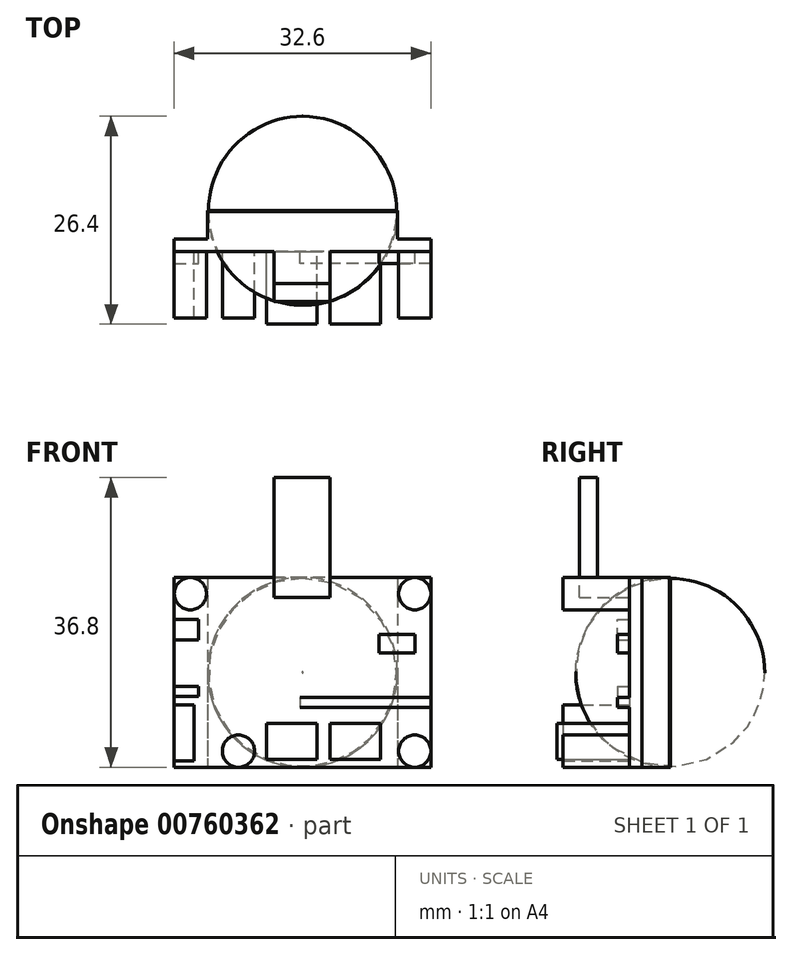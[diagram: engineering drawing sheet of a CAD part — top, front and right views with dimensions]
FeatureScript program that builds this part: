
annotation { "Feature Type Name" : "Feature", "Feature Type Description" : "" }
export const myFeature = defineFeature(function(context is Context, id is Id, definition is map)
    precondition{}
    {
        {
            var Q0;
            Q0=qCreatedBy(makeId("Front.planeOp"),FACE);
            var sketch = newSketch(context, id + "F0", { "sketchPlane" : qUnion([Q0])});
            skLineSegment(sketch, "E0.bottom", {"start": v(16.3, 12.05) * mm, "end": v(-16.3, 12.05) * mm});
            skLineSegment(sketch, "E0.top", {"start": v(16.3, -12.05) * mm, "end": v(-16.3, -12.05) * mm});
            skLineSegment(sketch, "E0.left", {"start": v(16.3, 12.05) * mm, "end": v(16.3, -12.05) * mm});
            skLineSegment(sketch, "E0.right", {"start": v(-16.3, 12.05) * mm, "end": v(-16.3, -12.05) * mm});
            skPoint(sketch, "E0.middle", {"position": v(0, 0) * mm});
            skLineSegment(sketch, "E1.bottom", {"start": v(12.05, 12.05) * mm, "end": v(-12.05, 12.05) * mm});
            skLineSegment(sketch, "E1.top", {"start": v(12.05, -12.05) * mm, "end": v(-12.05, -12.05) * mm});
            skLineSegment(sketch, "E1.left", {"start": v(12.05, 12.05) * mm, "end": v(12.05, -12.05) * mm});
            skLineSegment(sketch, "E1.right", {"start": v(-12.05, 12.05) * mm, "end": v(-12.05, -12.05) * mm});
            skCircle(sketch, "E2", {"center": v(0, 0) * mm, "radius": 12.05 * mm});
            skSolve(sketch);
        }
        {
            var Q0;
            Q0=qCreatedBy(makeId("Front.planeOp"),FACE);
            var sketch = newSketch(context, id + "F1", { "sketchPlane" : qUnion([Q0])});
            skCircle(sketch, "E3", {"center": v(-14.25, 10) * mm, "radius": 2.05 * mm});
            skCircle(sketch, "E4", {"center": v(14.25, 10) * mm, "radius": 2.05 * mm});
            skCircle(sketch, "E5", {"center": v(14.25, -10) * mm, "radius": 2.05 * mm});
            skCircle(sketch, "E6", {"center": v(-8.15, -10) * mm, "radius": 2.05 * mm});
            skLineSegment(sketch, "E7.bottom", {"start": v(-4.6, -6.45) * mm, "end": v(1.8, -6.45) * mm});
            skLineSegment(sketch, "E7.top", {"start": v(-4.6, -11.05) * mm, "end": v(1.8, -11.05) * mm});
            skLineSegment(sketch, "E7.left", {"start": v(-4.6, -6.45) * mm, "end": v(-4.6, -11.05) * mm});
            skLineSegment(sketch, "E7.right", {"start": v(1.8, -6.45) * mm, "end": v(1.8, -11.05) * mm});
            skLineSegment(sketch, "E8.bottom", {"start": v(3.5, -6.45) * mm, "end": v(9.9, -6.45) * mm});
            skLineSegment(sketch, "E8.top", {"start": v(3.5, -11.05) * mm, "end": v(9.9, -11.05) * mm});
            skLineSegment(sketch, "E8.left", {"start": v(3.5, -6.45) * mm, "end": v(3.5, -11.05) * mm});
            skLineSegment(sketch, "E8.right", {"start": v(9.9, -6.45) * mm, "end": v(9.9, -11.05) * mm});
            skLineSegment(sketch, "E9.bottom", {"start": v(-16.3, -4.15) * mm, "end": v(-13.8, -4.15) * mm});
            skLineSegment(sketch, "E9.top", {"start": v(-16.3, -11.25) * mm, "end": v(-13.8, -11.25) * mm});
            skLineSegment(sketch, "E9.left", {"start": v(-16.3, -4.15) * mm, "end": v(-16.3, -11.25) * mm});
            skLineSegment(sketch, "E9.right", {"start": v(-13.8, -4.15) * mm, "end": v(-13.8, -11.25) * mm});
            skLineSegment(sketch, "E10", {"start": v(-6.1, -8.53) * mm, "end": v(-6.1, -11.33) * mm, "construction": true});
            skLineSegment(sketch, "E11.bottom", {"start": v(-3.6, 9.55) * mm, "end": v(3.5, 9.55) * mm});
            skLineSegment(sketch, "E11.top", {"start": v(-3.6, 12.05) * mm, "end": v(3.5, 12.05) * mm});
            skLineSegment(sketch, "E11.left", {"start": v(-3.6, 9.55) * mm, "end": v(-3.6, 12.05) * mm});
            skLineSegment(sketch, "E11.right", {"start": v(3.5, 9.55) * mm, "end": v(3.5, 12.05) * mm});
            skLineSegment(sketch, "E12", {"start": v(12.2, -9.52) * mm, "end": v(12.2, -11.22) * mm, "construction": true});
            skLineSegment(sketch, "E13.bottom", {"start": v(9.7, 4.85) * mm, "end": v(14.3, 4.85) * mm});
            skLineSegment(sketch, "E13.top", {"start": v(9.7, 2.45) * mm, "end": v(14.3, 2.45) * mm});
            skLineSegment(sketch, "E13.left", {"start": v(9.7, 4.85) * mm, "end": v(9.7, 2.45) * mm});
            skLineSegment(sketch, "E13.right", {"start": v(14.3, 4.85) * mm, "end": v(14.3, 2.45) * mm});
            skLineSegment(sketch, "E14.bottom", {"start": v(16.3, -3.15) * mm, "end": v(-0.3, -3.15) * mm});
            skLineSegment(sketch, "E14.top", {"start": v(16.3, -4.45) * mm, "end": v(-0.3, -4.45) * mm});
            skLineSegment(sketch, "E14.left", {"start": v(16.3, -3.15) * mm, "end": v(16.3, -4.45) * mm});
            skLineSegment(sketch, "E14.right", {"start": v(-0.3, -3.15) * mm, "end": v(-0.3, -4.45) * mm});
            skLineSegment(sketch, "E15.bottom", {"start": v(-16.3, 4.15) * mm, "end": v(-13.2, 4.15) * mm});
            skLineSegment(sketch, "E15.top", {"start": v(-16.3, 6.75) * mm, "end": v(-13.2, 6.75) * mm});
            skLineSegment(sketch, "E15.left", {"start": v(-16.3, 4.15) * mm, "end": v(-16.3, 6.75) * mm});
            skLineSegment(sketch, "E15.right", {"start": v(-13.2, 4.15) * mm, "end": v(-13.2, 6.75) * mm});
            skLineSegment(sketch, "E16.bottom", {"start": v(-16.3, -1.75) * mm, "end": v(-13.2, -1.75) * mm});
            skLineSegment(sketch, "E16.top", {"start": v(-16.3, -3.05) * mm, "end": v(-13.2, -3.05) * mm});
            skLineSegment(sketch, "E16.left", {"start": v(-16.3, -1.75) * mm, "end": v(-16.3, -3.05) * mm});
            skLineSegment(sketch, "E16.right", {"start": v(-13.2, -1.75) * mm, "end": v(-13.2, -3.05) * mm});
            skSolve(sketch);
        }
        {
            var Q0;
            Q0=qSketchRegion(id+"F0",true);
            extrude(context, id + "F2", {"entities" : qUnion([Q0]), "oppositeDirection" : true, "depth" : 1.6 * mm});
        }
        {
            var Q0;
            {var subQ1=sQuery(id+"F0.wireOp",EDGE,"E1.top");var subQ3=sQuery(id+"F0.wireOp",EDGE,"E2");var subQ4=makeQuery(id+"F0.imprint","INTERSECT",VERTEX,{"derivedFrom":[subQ1,subQ3]});Q0=makeQuery(id+"F0.imprint","IMPRINT",FACE,{"disambiguationData":[TD([[makeQuery(id+"F0.imprint","IMPRINT",EDGE,{"disambiguationData":[TD([[subQ4,1.0]])],"derivedFrom":subQ3}),-1.0]])]});}
            var Q1;
            {var subQ1=sQuery(id+"F0.wireOp",EDGE,"E1.bottom");var subQ3=sQuery(id+"F0.wireOp",EDGE,"E2");var subQ4=makeQuery(id+"F0.imprint","INTERSECT",VERTEX,{"derivedFrom":[subQ1,subQ3]});Q1=makeQuery(id+"F0.imprint","IMPRINT",FACE,{"disambiguationData":[TD([[makeQuery(id+"F0.imprint","IMPRINT",EDGE,{"disambiguationData":[TD([[subQ4,-1.0]])],"derivedFrom":subQ3}),-1.0]])]});}
            var Q2;
            {var subQ0=sQuery(id+"F0.wireOp",EDGE,"E2");var subQ1=makeQuery(id+"F0.imprint","INTERSECT",VERTEX,{"derivedFrom":[sQuery(id+"F0.wireOp",EDGE,"E1.bottom"),subQ0]});Q2=makeQuery(id+"F0.imprint","IMPRINT",FACE,{"disambiguationData":[TD([[makeQuery(id+"F0.imprint","IMPRINT",EDGE,{"disambiguationData":[TD([[subQ1,1.0]])],"derivedFrom":subQ0}),1.0]])]});}
            var Q3;
            {var subQ1=sQuery(id+"F0.wireOp",EDGE,"E1.bottom");var subQ3=sQuery(id+"F0.wireOp",EDGE,"E2");var subQ4=makeQuery(id+"F0.imprint","INTERSECT",VERTEX,{"derivedFrom":[subQ1,subQ3]});Q3=makeQuery(id+"F0.imprint","IMPRINT",FACE,{"disambiguationData":[TD([[makeQuery(id+"F0.imprint","IMPRINT",EDGE,{"disambiguationData":[TD([[subQ4,1.0]])],"derivedFrom":subQ3}),-1.0]])]});}
            var Q4;
            {var subQ1=sQuery(id+"F0.wireOp",EDGE,"E1.top");var subQ3=sQuery(id+"F0.wireOp",EDGE,"E2");var subQ4=makeQuery(id+"F0.imprint","INTERSECT",VERTEX,{"derivedFrom":[subQ1,subQ3]});Q4=makeQuery(id+"F0.imprint","IMPRINT",FACE,{"disambiguationData":[TD([[makeQuery(id+"F0.imprint","IMPRINT",EDGE,{"disambiguationData":[TD([[subQ4,-1.0]])],"derivedFrom":subQ3}),-1.0]])]});}
            extrude(context, id + "F3", {"entities" : qUnion([Q0, Q1, Q2, Q3, Q4]), "operationType" : NewBodyOperationType.ADD, "oppositeDirection" : true, "depth" : 5.1 * mm});
        }
        {
            var Q0;
            {var subQ0=sQuery(id+"F0.wireOp",EDGE,"E2");var subQ1=makeQuery(id+"F0.imprint","INTERSECT",VERTEX,{"derivedFrom":[sQuery(id+"F0.wireOp",EDGE,"E1.bottom"),subQ0]});Q0=makeQuery(id+"F0.imprint","IMPRINT",FACE,{"disambiguationData":[TD([[makeQuery(id+"F0.imprint","IMPRINT",EDGE,{"disambiguationData":[TD([[subQ1,1.0]])],"derivedFrom":subQ0}),1.0]])]});}
            extrude(context, id + "F4", {"entities" : qUnion([Q0]), "operationType" : NewBodyOperationType.ADD, "oppositeDirection" : true, "depth" : 17.2 * mm});
        }
        {
            var Q0;
            Q0=makeQuery(id+"F4.opExtrude","CAP_EDGE",EDGE,{"disambiguationData":[OSD([sQuery(id+"F0.wireOp",EDGE,"E2")])],"isStart":false});
            fillet(context, id + "F5", {"entities" : qUnion([Q0]), "radius" : 12 * mm, "tangentPropagation" : true, "allowEdgeOverflow" : false});
        }
        {
            var Q0;
            Q0=makeQuery(id+"F1.imprint","IMPRINT",FACE,{"disambiguationData":[TD([[makeQuery(id+"F1.imprint","IMPRINT",EDGE,{"derivedFrom":sQuery(id+"F1.wireOp",EDGE,"E3")}),1.0]])]});
            var Q1;
            Q1=makeQuery(id+"F1.imprint","IMPRINT",FACE,{"disambiguationData":[TD([[makeQuery(id+"F1.imprint","IMPRINT",EDGE,{"derivedFrom":sQuery(id+"F1.wireOp",EDGE,"E4")}),1.0]])]});
            var Q2;
            Q2=makeQuery(id+"F1.imprint","IMPRINT",FACE,{"disambiguationData":[TD([[makeQuery(id+"F1.imprint","IMPRINT",EDGE,{"derivedFrom":sQuery(id+"F1.wireOp",EDGE,"E5")}),1.0]])]});
            var Q3;
            Q3=makeQuery(id+"F1.imprint","IMPRINT",FACE,{"disambiguationData":[TD([[makeQuery(id+"F1.imprint","IMPRINT",EDGE,{"derivedFrom":sQuery(id+"F1.wireOp",EDGE,"E6")}),1.0]])]});
            var Q4;
            Q4=makeQuery(id+"F1.imprint","IMPRINT",FACE,{"disambiguationData":[TD([[makeQuery(id+"F1.imprint","IMPRINT",EDGE,{"derivedFrom":sQuery(id+"F1.wireOp",EDGE,"E9.bottom")}),-1.0]])]});
            extrude(context, id + "F6", {"entities" : qUnion([Q0, Q1, Q2, Q3, Q4]), "operationType" : NewBodyOperationType.ADD, "depth" : 8.4 * mm, "offsetDistance" : 25 * mm});
        }
        {
            var Q0;
            Q0=makeQuery(id+"F1.imprint","IMPRINT",FACE,{"disambiguationData":[TD([[makeQuery(id+"F1.imprint","IMPRINT",EDGE,{"derivedFrom":sQuery(id+"F1.wireOp",EDGE,"E7.bottom")}),-1.0]])]});
            var Q1;
            Q1=makeQuery(id+"F1.imprint","IMPRINT",FACE,{"disambiguationData":[TD([[makeQuery(id+"F1.imprint","IMPRINT",EDGE,{"derivedFrom":sQuery(id+"F1.wireOp",EDGE,"E8.bottom")}),-1.0]])]});
            extrude(context, id + "F7", {"entities" : qUnion([Q0, Q1]), "operationType" : NewBodyOperationType.ADD, "depth" : 9.2 * mm});
        }
        {
            var Q0;
            Q0=makeQuery(id+"F1.imprint","IMPRINT",FACE,{"disambiguationData":[TD([[makeQuery(id+"F1.imprint","IMPRINT",EDGE,{"derivedFrom":sQuery(id+"F1.wireOp",EDGE,"E16.bottom")}),-1.0]])]});
            var Q1;
            Q1=makeQuery(id+"F1.imprint","IMPRINT",FACE,{"disambiguationData":[TD([[makeQuery(id+"F1.imprint","IMPRINT",EDGE,{"derivedFrom":sQuery(id+"F1.wireOp",EDGE,"E13.bottom")}),-1.0]])]});
            var Q2;
            Q2=makeQuery(id+"F1.imprint","IMPRINT",FACE,{"disambiguationData":[TD([[makeQuery(id+"F1.imprint","IMPRINT",EDGE,{"derivedFrom":sQuery(id+"F1.wireOp",EDGE,"E14.bottom")}),1.0]])]});
            var Q3;
            Q3=makeQuery(id+"F1.imprint","IMPRINT",FACE,{"disambiguationData":[TD([[makeQuery(id+"F1.imprint","IMPRINT",EDGE,{"derivedFrom":sQuery(id+"F1.wireOp",EDGE,"E15.bottom")}),1.0]])]});
            extrude(context, id + "F8", {"entities" : qUnion([Q0, Q1, Q2, Q3]), "operationType" : NewBodyOperationType.ADD, "depth" : 1.5 * mm});
        }
        {
            var Q0;
            Q0=makeQuery(id+"F1.imprint","IMPRINT",FACE,{"disambiguationData":[TD([[makeQuery(id+"F1.imprint","IMPRINT",EDGE,{"derivedFrom":sQuery(id+"F1.wireOp",EDGE,"E11.bottom")}),1.0]])]});
            extrude(context, id + "F9", {"entities" : qUnion([Q0]), "operationType" : NewBodyOperationType.ADD, "depth" : 6.35 * mm, "offsetDistance" : 25 * mm});
        }
        {
            var Q0;
            {var subQ0=sQuery(id+"F0.wireOp",EDGE,"E1.bottom");Q0=makeQuery(id+"F9.boolean.opBoolean","MERGE",FACE,{"derivedFrom":[makeQuery(id+"F3.boolean.opBoolean","MERGE",FACE,{"derivedFrom":[makeQuery(id+"F2.opExtrude","SWEPT_FACE",FACE,{"disambiguationData":[OSD([sQuery(id+"F0.wireOp",EDGE,"E0.bottom"),subQ0])]}),makeQuery(id+"F3.opExtrude","SWEPT_FACE",FACE,{"disambiguationData":[OSD([subQ0])]})]}),makeQuery(id+"F9.opExtrude","SWEPT_FACE",FACE,{"disambiguationData":[OSD([sQuery(id+"F1.wireOp",EDGE,"E11.top")])]})]});}
            var sketch = newSketch(context, id + "F10", { "sketchPlane" : qUnion([Q0])});
            skLineSegment(sketch, "E17.bottom", {"start": v(-3.6, -4.05) * mm, "end": v(3.5, -4.05) * mm});
            skLineSegment(sketch, "E17.top", {"start": v(-3.6, -6.35) * mm, "end": v(3.5, -6.35) * mm});
            skLineSegment(sketch, "E17.left", {"start": v(-3.6, -4.05) * mm, "end": v(-3.6, -6.35) * mm});
            skLineSegment(sketch, "E17.right", {"start": v(3.5, -4.05) * mm, "end": v(3.5, -6.35) * mm});
            skSolve(sketch);
        }
        {
            var Q0;
            Q0 = qSketchRegion(id + "F10", true);
            extrude(context, id + "F11", {"entities" : qUnion([Q0]), "operationType" : NewBodyOperationType.ADD, "depth" : 12.7 * mm, "offsetDistance" : 25 * mm});
        }
    });
